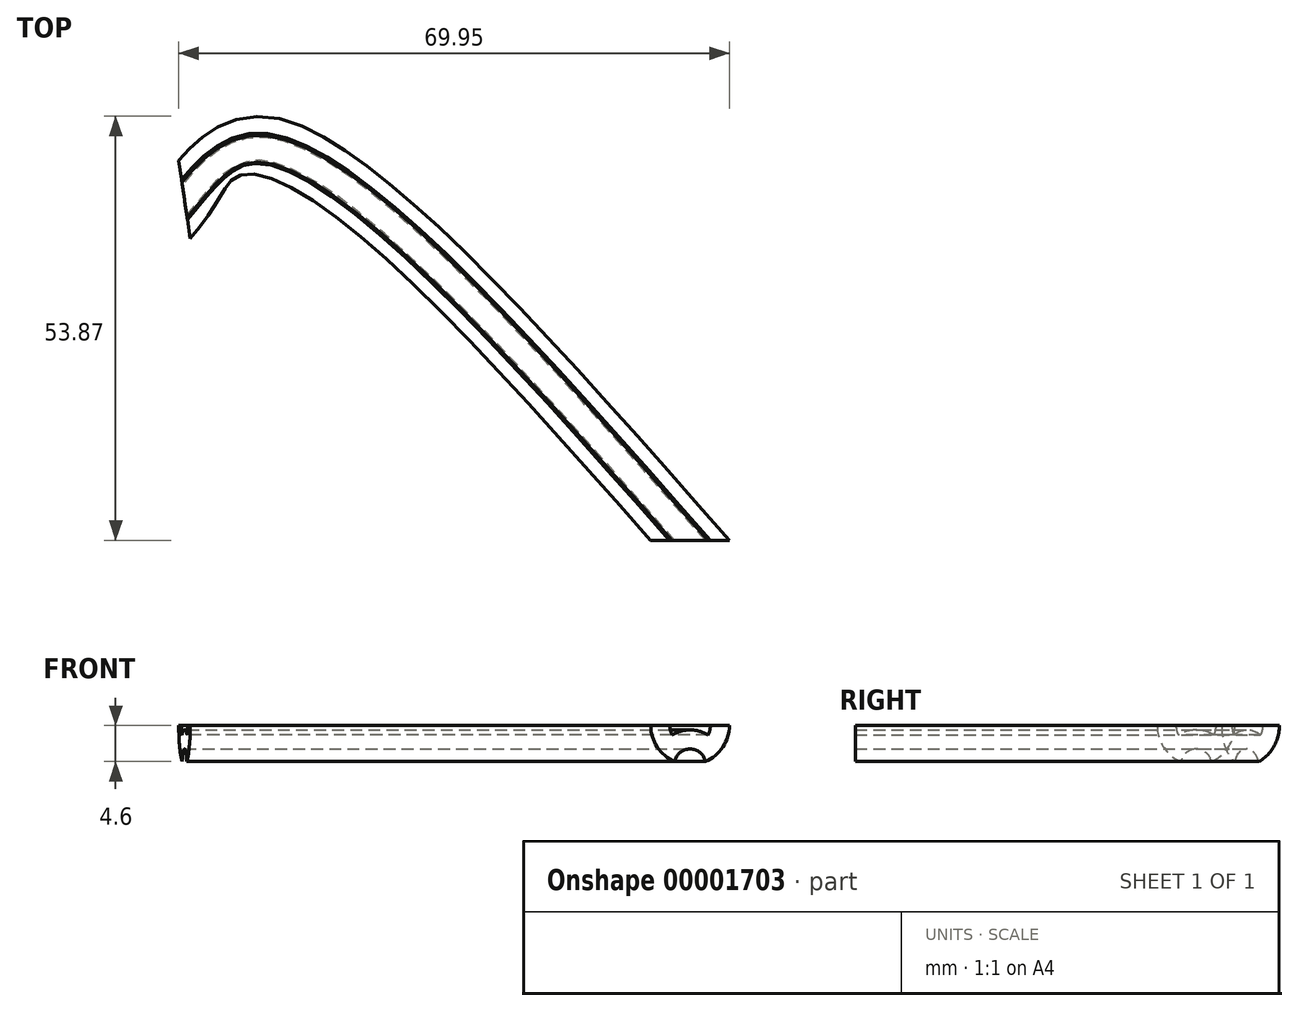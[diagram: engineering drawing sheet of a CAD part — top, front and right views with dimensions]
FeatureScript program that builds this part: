
annotation { "Feature Type Name" : "Feature", "Feature Type Description" : "" }
export const myFeature = defineFeature(function(context is Context, id is Id, definition is map)
    precondition{}
    {
        {
            var Q0;
            Q0=qCreatedBy(makeId("Top.planeOp"),FACE);
            var sketch = newSketch(context, id + "F0", { "sketchPlane" : qUnion([Q0])});
            skLineSegment(sketch, "E0", {"start": v(0, 0) * mm, "end": v(0, 46.1) * mm});
            skFitSpline(sketch, "E1", {"points": [v(0, 0) * mm, v(-53.97, 49.6) * mm, v(-64.22, 43.28) * mm], "startDerivative": vector(-90.18, 102.32) * mm, "endDerivative": vector(-29.74, -35.14) * mm});
            skSolve(sketch);
        }
        {
            var Q0;
            Q0=qCreatedBy(makeId("Front.planeOp"),FACE);
            var sketch = newSketch(context, id + "F1", { "sketchPlane" : qUnion([Q0])});
            skArc(sketch, "E2", {"start": v(-5, 0) * mm, "mid": v(-4.17, -2.76) * mm, "end": v(-1.96, -4.6) * mm});
            skArc(sketch, "E3", {"start": v(1.96, -4.6) * mm, "mid": v(0, -3) * mm, "end": v(-1.96, -4.6) * mm});
            skArc(sketch, "E4.trimOffspring", {"start": v(1.96, -4.6) * mm, "mid": v(4.17, -2.76) * mm, "end": v(5, 0) * mm});
            skLineSegment(sketch, "E5", {"start": v(0, 0) * mm, "end": v(0, -12.35) * mm, "construction": true});
            skArc(sketch, "E6.0", {"start": v(2.28, -1.22) * mm, "mid": v(2.5, -0.63) * mm, "end": v(2.58, 0) * mm});
            skArc(sketch, "E6.1", {"start": v(2.28, -1.22) * mm, "mid": v(0, -0.58) * mm, "end": v(-2.28, -1.22) * mm});
            skArc(sketch, "E6.2", {"start": v(-2.58, 0) * mm, "mid": v(-2.5, -0.63) * mm, "end": v(-2.28, -1.22) * mm});
            skLineSegment(sketch, "E7", {"start": v(-5, 0) * mm, "end": v(-2.58, 0) * mm});
            skLineSegment(sketch, "E8", {"start": v(2.58, 0) * mm, "end": v(5, 0) * mm});
            skSolve(sketch);
        }
        {
            var Q0;
            Q0=makeQuery(id+"F1.imprint","IMPRINT",FACE,{"disambiguationData":[TD([[makeQuery(id+"F1.imprint","IMPRINT",EDGE,{"derivedFrom":sQuery(id+"F1.wireOp",EDGE,"E2")}),1.0]])]});
            var Q1;
            Q1=sQuery(id+"F0.wireOp",EDGE,"E1");
            sweep(context, id + "F2", {"profiles" : qUnion([Q0]), "path" : qUnion([Q1])});
        }
    });
